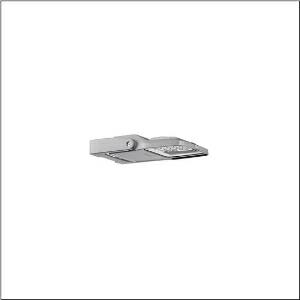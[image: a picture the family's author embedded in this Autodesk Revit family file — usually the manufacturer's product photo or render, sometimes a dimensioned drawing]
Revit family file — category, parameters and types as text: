
# Revit family: floodlight_fl_21_iq_micro___pl61_5xa7761a2c2a_8a4e
name_source: partatom
category: Lighting Fixtures
units: mm (PartAtom-declared; Revit-internal decimal feet)

## family parameters
Cut with Voids When Loaded = No
Host = Face
Light Source = No
Part Type = Normal
Room Calculation Point = No
Round Connector Dimension = Use Diameter
Shared = No

## types (1)
- --- (1 x LED, 2910 lm, 23.1 W, 3000K)
    Apparent Load = 23 VA
    CIE Flux Codes = 33 65 98 100 100
    Color Rendering = 70
    Color Temperature = 3000K
    Default Elevation = 1800 mm
    Description = Floodlight FL 21 iQ micro, floodlight, primary light control with lens, of PMMA, primary optical cover: protective disc, of toughened safety glass, transparent, light distribution: PL61, light emission: direct distribution, installation type: surface-mounted, LED, High Power LED, rated luminous flux: 2.910lm, luminous efficacy: 126lm/W, light colour: 730, colour temperature: 3000K, control gear: iQ Comfort/DALI, control: optimised constant luminous flux control (CLO 2.0), Desk-Remote (wireless, voltage-free reading and setting of iQ features in the workshop via application-optimized NFC function/RFID function), Light-Fading, Smart-Wire, Night-Set, Lumen-Switch, Temp-Guard, Auto-Match, with terminal, 6-pole, mains connection: 220..240V, AC, 50/60Hz, start of lifetime: 23W, end of service life: 24W, reduction: 11W, luminaire housing, of diecast aluminium, powder-coated, Siteco® metallic grey (DB 702S), corrosivity category C5 mid according to DIN EN ISO 12944, suitable for swimming pools, chlorine-resistant, sealing non-destructively replaceable, design bracket, of diecast aluminium, powder-coated, Siteco® metallic grey (DB 702S), protection rating (complete): IP66, insulation class (complete): insulation class II (safety insulation), certification: CE, ENEC, VDE, protection symbol: D, impact resistance: IK07, permissible operating ambient temperature: -40..+40°C, permissible operating ambient temperature for outdoor applications: -40..+50°C, standard: DIN EN 12944, LABS conformity tested according to VDMA 24364:2018-05, packaging unit: 1 piece

Light Distribution: PL61
    Height = 65 mm
    Lamp = 1 x LED
    Lamp Light Flux = 2910 lm
    Lamp Power = 23.1 W
    Lamp count = 1
    Length = 312 mm
    Luminous efficacy = 126 lm/W
    Manufacturer = Siteco
    ModVariant = No
    Model = 5XA7761A2C2A
    Mounting Place = Wall
    Mounting Type = Surface mounted
    Number of Poles = 1
    OnlyDefault = Yes
    Power Factor = 1
    Product Name = Floodlight FL 21 iQ micro | PL61
    Product group = floodlight | wall mounted
    ProductGroupID = 2001
    Protection Class = Protection class II
    Protection Degree = IP 66
    RLX_Detail_Level = 1
    RLX_Emergency_Light_Flux = 0 lm
    RLX_Emergency_Type = 0
    RLX_Emergency_Type_DB = No
    RlxData = <blob elided: 97609 chars, md5=a44a5c29>
    Socket = socket
    Standby Power = 0 W
    System Light Flux = 2910 lm
    System Power = 23 W
    Type Comments = factory setting: luminous flux: 100 % | dim-lin: 254 | 455 mA
    Type Image = l_1006878.jpg
    URL = http://relux.com
    VarID = @adj_194656
    Voltage = 0 V
    Weight = 0.00 kg
    Width = 230 mm

## geometry (parser evidence)
native form markers: Blend x4, Sweep x11
no freeform markers — native parametric forms only
